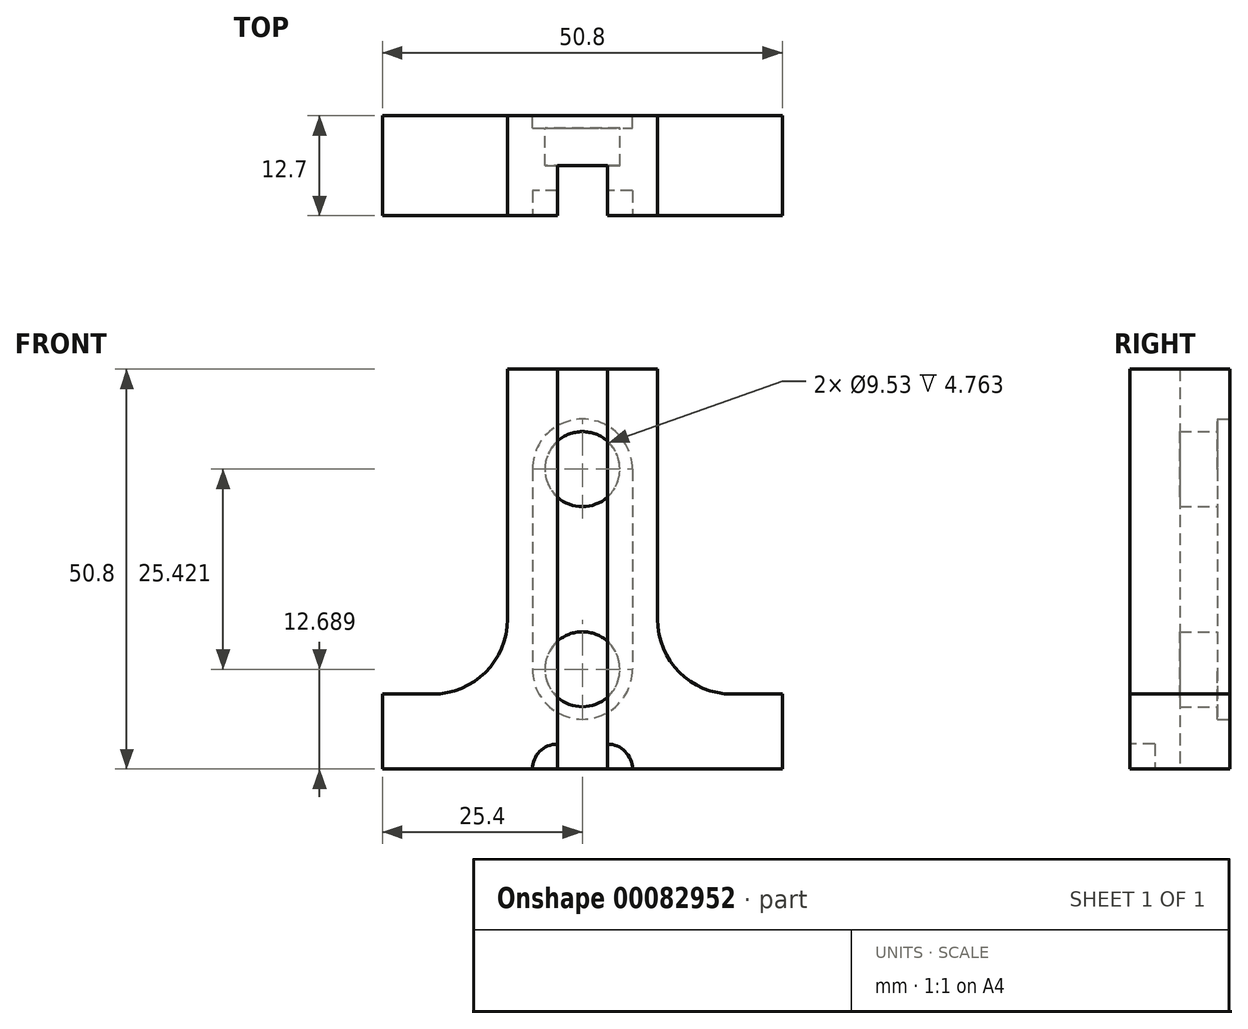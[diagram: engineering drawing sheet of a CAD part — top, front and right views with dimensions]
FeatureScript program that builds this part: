
annotation { "Feature Type Name" : "Feature", "Feature Type Description" : "" }
export const myFeature = defineFeature(function(context is Context, id is Id, definition is map)
    precondition{}
    {
        {
            var Q0;
            Q0=qCreatedBy(makeId("Front.planeOp"),FACE);
            var sketch = newSketch(context, id + "F0", { "sketchPlane" : qUnion([Q0])});
            skLineSegment(sketch, "E0.bottom", {"start": v(9.53, 25.4) * mm, "end": v(-9.53, 25.4) * mm});
            skLineSegment(sketch, "E0.top", {"start": v(25.4, -25.4) * mm, "end": v(-25.4, -25.4) * mm});
            skLineSegment(sketch, "E0.left", {"start": v(25.4, -15.88) * mm, "end": v(25.4, -25.4) * mm});
            skLineSegment(sketch, "E0.right", {"start": v(-25.4, -15.88) * mm, "end": v(-25.4, -25.4) * mm});
            skPoint(sketch, "E0.middle", {"position": v(0, 0) * mm});
            skLineSegment(sketch, "E1", {"start": v(-25.4, -15.88) * mm, "end": v(-9.53, -15.88) * mm});
            skLineSegment(sketch, "E2", {"start": v(-9.52, -15.88) * mm, "end": v(-9.53, 25.4) * mm});
            skLineSegment(sketch, "E3", {"start": v(25.4, -15.88) * mm, "end": v(9.53, -15.88) * mm});
            skLineSegment(sketch, "E4", {"start": v(9.53, -15.88) * mm, "end": v(9.53, 25.4) * mm});
            skPoint(sketch, "E5.orphan", {"position": v(-25.4, 25.4) * mm});
            skPoint(sketch, "E6.orphan", {"position": v(25.4, 25.4) * mm});
            skLineSegment(sketch, "E7", {"start": v(-3.17, 25.4) * mm, "end": v(-3.18, -25.4) * mm});
            skLineSegment(sketch, "E8", {"start": v(3.18, 25.4) * mm, "end": v(3.18, -25.4) * mm});
            skSolve(sketch);
        }
        {
            var Q0;
            {var subQ0=sQuery(id+"F0.wireOp",EDGE,"E0.right");Q0=makeQuery(id+"F0.imprint","IMPRINT",FACE,{"disambiguationData":[TD([[makeQuery(id+"F0.imprint","IMPRINT",EDGE,{"derivedFrom":subQ0}),1.0]])]});}
            var Q1;
            {var subQ0=sQuery(id+"F0.wireOp",EDGE,"E0.left");Q1=makeQuery(id+"F0.imprint","IMPRINT",FACE,{"disambiguationData":[TD([[makeQuery(id+"F0.imprint","IMPRINT",EDGE,{"derivedFrom":subQ0}),-1.0]])]});}
            extrude(context, id + "F1", {"entities" : qUnion([Q0, Q1]), "depth" : 6.35 * mm});
        }
        {
            var Q0;
            {var subQ0=sQuery(id+"F0.wireOp",EDGE,"E0.left");Q0=makeQuery(id+"F0.imprint","IMPRINT",FACE,{"disambiguationData":[TD([[makeQuery(id+"F0.imprint","IMPRINT",EDGE,{"derivedFrom":subQ0}),-1.0]])]});}
            var Q1;
            {var subQ0=sQuery(id+"F0.wireOp",EDGE,"E7");Q1=makeQuery(id+"F0.imprint","IMPRINT",FACE,{"disambiguationData":[TD([[makeQuery(id+"F0.imprint","IMPRINT",EDGE,{"derivedFrom":subQ0}),1.0]])]});}
            var Q2;
            {var subQ0=sQuery(id+"F0.wireOp",EDGE,"E0.right");Q2=makeQuery(id+"F0.imprint","IMPRINT",FACE,{"disambiguationData":[TD([[makeQuery(id+"F0.imprint","IMPRINT",EDGE,{"derivedFrom":subQ0}),1.0]])]});}
            extrude(context, id + "F2", {"entities" : qUnion([Q0, Q1, Q2]), "oppositeDirection" : true, "depth" : 6.35 * mm});
        }
        {
            var Q0;
            Q0=makeQuery(id+"F1.opExtrude","SWEPT_BODY",BODY,{"disambiguationData":[OSD([sQuery(id+"F0.wireOp",EDGE,"E0.bottom"),sQuery(id+"F0.wireOp",EDGE,"E0.top"),sQuery(id+"F0.wireOp",EDGE,"E0.left"),sQuery(id+"F0.wireOp",EDGE,"E3"),sQuery(id+"F0.wireOp",EDGE,"E4"),sQuery(id+"F0.wireOp",EDGE,"E8")])]});
            var Q1;
            Q1=makeQuery(id+"F1.opExtrude","SWEPT_BODY",BODY,{"disambiguationData":[OSD([sQuery(id+"F0.wireOp",EDGE,"E0.bottom"),sQuery(id+"F0.wireOp",EDGE,"E0.top"),sQuery(id+"F0.wireOp",EDGE,"E0.right"),sQuery(id+"F0.wireOp",EDGE,"E1"),sQuery(id+"F0.wireOp",EDGE,"E2"),sQuery(id+"F0.wireOp",EDGE,"E7")])]});
            var Q2;
            Q2=makeQuery(id+"F2.opExtrude","SWEPT_BODY",BODY,{"disambiguationData":[OSD([sQuery(id+"F0.wireOp",EDGE,"E0.bottom"),sQuery(id+"F0.wireOp",EDGE,"E0.top"),sQuery(id+"F0.wireOp",EDGE,"E0.left"),sQuery(id+"F0.wireOp",EDGE,"E0.right"),sQuery(id+"F0.wireOp",EDGE,"E1"),sQuery(id+"F0.wireOp",EDGE,"E2"),sQuery(id+"F0.wireOp",EDGE,"E3"),sQuery(id+"F0.wireOp",EDGE,"E4")])]});
            booleanBodies(context, id + "F3", {"operationType" : BooleanOperationType.UNION, "tools" : qUnion([Q0, Q1, Q2])});
        }
        {
            var Q0;
            {var subQ0=sQuery(id+"F0.wireOp",EDGE,"E4");var subQ1=sQuery(id+"F0.wireOp",EDGE,"E3");Q0=makeQuery(id+"F3.opBoolean","MERGE",EDGE,{"derivedFrom":[makeQuery(id+"F1.opExtrude","SWEPT_EDGE",EDGE,{"disambiguationData":[OSD([subQ1,subQ0])]}),makeQuery(id+"F2.opExtrude","SWEPT_EDGE",EDGE,{"disambiguationData":[OSD([subQ1,subQ0])]})]});}
            var Q1;
            {var subQ0=sQuery(id+"F0.wireOp",EDGE,"E2");var subQ1=sQuery(id+"F0.wireOp",EDGE,"E1");Q1=makeQuery(id+"F3.opBoolean","MERGE",EDGE,{"derivedFrom":[makeQuery(id+"F1.opExtrude","SWEPT_EDGE",EDGE,{"disambiguationData":[OSD([subQ1,subQ0])]}),makeQuery(id+"F2.opExtrude","SWEPT_EDGE",EDGE,{"disambiguationData":[OSD([subQ1,subQ0])]})]});}
            fillet(context, id + "F4", {"entities" : qUnion([Q0, Q1]), "radius" : 9.52 * mm, "tangentPropagation" : true, "allowEdgeOverflow" : false});
        }
        {
            var Q0;
            Q0=makeQuery(id+"F2.opExtrude","CAP_FACE",FACE,{"disambiguationData":[OSD([sQuery(id+"F0.wireOp",EDGE,"E0.bottom"),sQuery(id+"F0.wireOp",EDGE,"E0.top"),sQuery(id+"F0.wireOp",EDGE,"E0.left"),sQuery(id+"F0.wireOp",EDGE,"E0.right"),sQuery(id+"F0.wireOp",EDGE,"E1"),sQuery(id+"F0.wireOp",EDGE,"E2"),sQuery(id+"F0.wireOp",EDGE,"E3"),sQuery(id+"F0.wireOp",EDGE,"E4")])],"isStart":false});
            var sketch = newSketch(context, id + "F5", { "sketchPlane" : qUnion([Q0])});
            skLineSegment(sketch, "E9.left", {"start": v(6.35, 12.69) * mm, "end": v(6.35, -12.71) * mm});
            skLineSegment(sketch, "E9.right", {"start": v(-6.35, 12.71) * mm, "end": v(-6.35, -12.69) * mm});
            skPoint(sketch, "E9.middle", {"position": v(0, 0) * mm});
            skArc(sketch, "E10", {"start": v(-6.35, 12.71) * mm, "mid": v(0.01, 19.06) * mm, "end": v(6.35, 12.69) * mm});
            skArc(sketch, "E11", {"start": v(6.35, -12.71) * mm, "mid": v(-0.01, -19.06) * mm, "end": v(-6.35, -12.69) * mm});
            skCircle(sketch, "E12", {"center": v(0, 12.71) * mm, "radius": 4.76 * mm});
            skCircle(sketch, "E13", {"center": v(0, -12.71) * mm, "radius": 4.76 * mm});
            skSolve(sketch);
        }
        {
            var Q0;
            Q0=makeQuery(id+"F5.imprint","IMPRINT",FACE,{"disambiguationData":[TD([[makeQuery(id+"F5.imprint","IMPRINT",EDGE,{"derivedFrom":sQuery(id+"F5.wireOp",EDGE,"E12")}),1.0]])]});
            var Q1;
            Q1=makeQuery(id+"F5.imprint","IMPRINT",FACE,{"disambiguationData":[TD([[makeQuery(id+"F5.imprint","IMPRINT",EDGE,{"derivedFrom":sQuery(id+"F5.wireOp",EDGE,"E13")}),1.0]])]});
            extrude(context, id + "F6", {"entities" : qUnion([Q0, Q1]), "operationType" : NewBodyOperationType.REMOVE, "oppositeDirection" : true, "depth" : 6.35 * mm});
        }
        {
            var Q0;
            Q0=makeQuery(id+"F5.imprint","IMPRINT",FACE,{"disambiguationData":[TD([[makeQuery(id+"F5.imprint","IMPRINT",EDGE,{"derivedFrom":sQuery(id+"F5.wireOp",EDGE,"E9.left")}),-1.0]])]});
            extrude(context, id + "F7", {"entities" : qUnion([Q0]), "operationType" : NewBodyOperationType.REMOVE, "oppositeDirection" : true, "depth" : 1.59 * mm});
        }
        {
            var Q0;
            Q0=makeQuery(id+"F1.opExtrude","CAP_FACE",FACE,{"disambiguationData":[OSD([sQuery(id+"F0.wireOp",EDGE,"E0.bottom"),sQuery(id+"F0.wireOp",EDGE,"E0.top"),sQuery(id+"F0.wireOp",EDGE,"E0.right"),sQuery(id+"F0.wireOp",EDGE,"E1"),sQuery(id+"F0.wireOp",EDGE,"E2"),sQuery(id+"F0.wireOp",EDGE,"E7")])],"isStart":false});
            var sketch = newSketch(context, id + "F8", { "sketchPlane" : qUnion([Q0])});
            skCircle(sketch, "E14", {"center": v(-3.18, -25.4) * mm, "radius": 3.18 * mm});
            skSolve(sketch);
        }
        {
            var Q0;
            {var subQ0=sQuery(id+"F8.wireOp",EDGE,"E14");var subQ2=sQuery(id+"F0.wireOp",EDGE,"E7");var subQ5=makeQuery(id+"F1.opExtrude","CAP_EDGE",EDGE,{"disambiguationData":[OSD([subQ2])],"isStart":false});var subQ6=makeQuery(id+"F8.imprint","INTERSECT",VERTEX,{"derivedFrom":[subQ5,subQ0]});Q0=makeQuery(id+"F8.imprint","IMPRINT",FACE,{"disambiguationData":[TD([[makeQuery(id+"F8.imprint","IMPRINT",EDGE,{"disambiguationData":[TD([[subQ6,-1.0]])],"derivedFrom":subQ0}),1.0]])]});}
            extrude(context, id + "F9", {"entities" : qUnion([Q0]), "operationType" : NewBodyOperationType.REMOVE, "oppositeDirection" : true, "depth" : 3.17 * mm});
        }
        {
            var Q0;
            Q0=makeQuery(id+"F1.opExtrude","CAP_FACE",FACE,{"disambiguationData":[OSD([sQuery(id+"F0.wireOp",EDGE,"E0.bottom"),sQuery(id+"F0.wireOp",EDGE,"E0.top"),sQuery(id+"F0.wireOp",EDGE,"E0.left"),sQuery(id+"F0.wireOp",EDGE,"E3"),sQuery(id+"F0.wireOp",EDGE,"E4"),sQuery(id+"F0.wireOp",EDGE,"E8")])],"isStart":false});
            var sketch = newSketch(context, id + "F10", { "sketchPlane" : qUnion([Q0])});
            skCircle(sketch, "E15", {"center": v(3.18, -25.4) * mm, "radius": 3.18 * mm});
            skSolve(sketch);
        }
        {
            var Q0;
            {var subQ0=sQuery(id+"F10.wireOp",EDGE,"E15");var subQ2=sQuery(id+"F0.wireOp",EDGE,"E8");var subQ5=makeQuery(id+"F1.opExtrude","CAP_EDGE",EDGE,{"disambiguationData":[OSD([subQ2])],"isStart":false});var subQ6=makeQuery(id+"F10.imprint","INTERSECT",VERTEX,{"derivedFrom":[subQ5,subQ0]});Q0=makeQuery(id+"F10.imprint","IMPRINT",FACE,{"disambiguationData":[TD([[makeQuery(id+"F10.imprint","IMPRINT",EDGE,{"disambiguationData":[TD([[subQ6,1.0]])],"derivedFrom":subQ0}),1.0]])]});}
            extrude(context, id + "F11", {"entities" : qUnion([Q0]), "operationType" : NewBodyOperationType.REMOVE, "oppositeDirection" : true, "depth" : 3.17 * mm});
        }
        {
            var Q0;
            Q0=makeQuery(id+"F5.imprint","IMPRINT",FACE,{"disambiguationData":[TD([[makeQuery(id+"F5.imprint","IMPRINT",EDGE,{"derivedFrom":sQuery(id+"F5.wireOp",EDGE,"E9.left")}),-1.0]])]});
            var Q1;
            Q1=makeQuery(id+"F5.imprint","IMPRINT",FACE,{"disambiguationData":[TD([[makeQuery(id+"F5.imprint","IMPRINT",EDGE,{"derivedFrom":sQuery(id+"F5.wireOp",EDGE,"E12")}),1.0]])]});
            var Q2;
            Q2=makeQuery(id+"F5.imprint","IMPRINT",FACE,{"disambiguationData":[TD([[makeQuery(id+"F5.imprint","IMPRINT",EDGE,{"derivedFrom":sQuery(id+"F5.wireOp",EDGE,"E13")}),1.0]])]});
            extrude(context, id + "F12", {"entities" : qUnion([Q0, Q1, Q2]), "oppositeDirection" : true, "depth" : 1.59 * mm});
        }
        {
            var Q0;
            Q0=makeQuery(id+"F7.boolean.opBoolean","COPY",FACE,{"derivedFrom":makeQuery(id+"F7.opExtrude","CAP_FACE",FACE,{"disambiguationData":[OSD([sQuery(id+"F5.wireOp",EDGE,"E9.left"),sQuery(id+"F5.wireOp",EDGE,"E9.right"),sQuery(id+"F5.wireOp",EDGE,"E10"),sQuery(id+"F5.wireOp",EDGE,"E11"),sQuery(id+"F5.wireOp",EDGE,"E12"),sQuery(id+"F5.wireOp",EDGE,"E13")])],"isStart":false})});
            var sketch = newSketch(context, id + "F13", { "sketchPlane" : qUnion([Q0])});
            skCircle(sketch, "E16", {"center": v(0, 12.71) * mm, "radius": 4.76 * mm});
            skCircle(sketch, "E17", {"center": v(0, -12.71) * mm, "radius": 4.76 * mm});
            skSolve(sketch);
        }
        {
            var Q0;
            Q0=makeQuery(id+"F13.imprint","IMPRINT",FACE,{"disambiguationData":[TD([[makeQuery(id+"F13.imprint","IMPRINT",EDGE,{"derivedFrom":sQuery(id+"F13.wireOp",EDGE,"E16")}),1.0]])]});
            extrude(context, id + "F14", {"entities" : qUnion([Q0]), "oppositeDirection" : true, "depth" : 4.76 * mm});
        }
        {
            var Q0;
            Q0=makeQuery(id+"F13.imprint","IMPRINT",FACE,{"disambiguationData":[TD([[makeQuery(id+"F13.imprint","IMPRINT",EDGE,{"derivedFrom":sQuery(id+"F13.wireOp",EDGE,"E17")}),1.0]])]});
            extrude(context, id + "F15", {"entities" : qUnion([Q0]), "oppositeDirection" : true, "depth" : 4.76 * mm});
        }
    });
